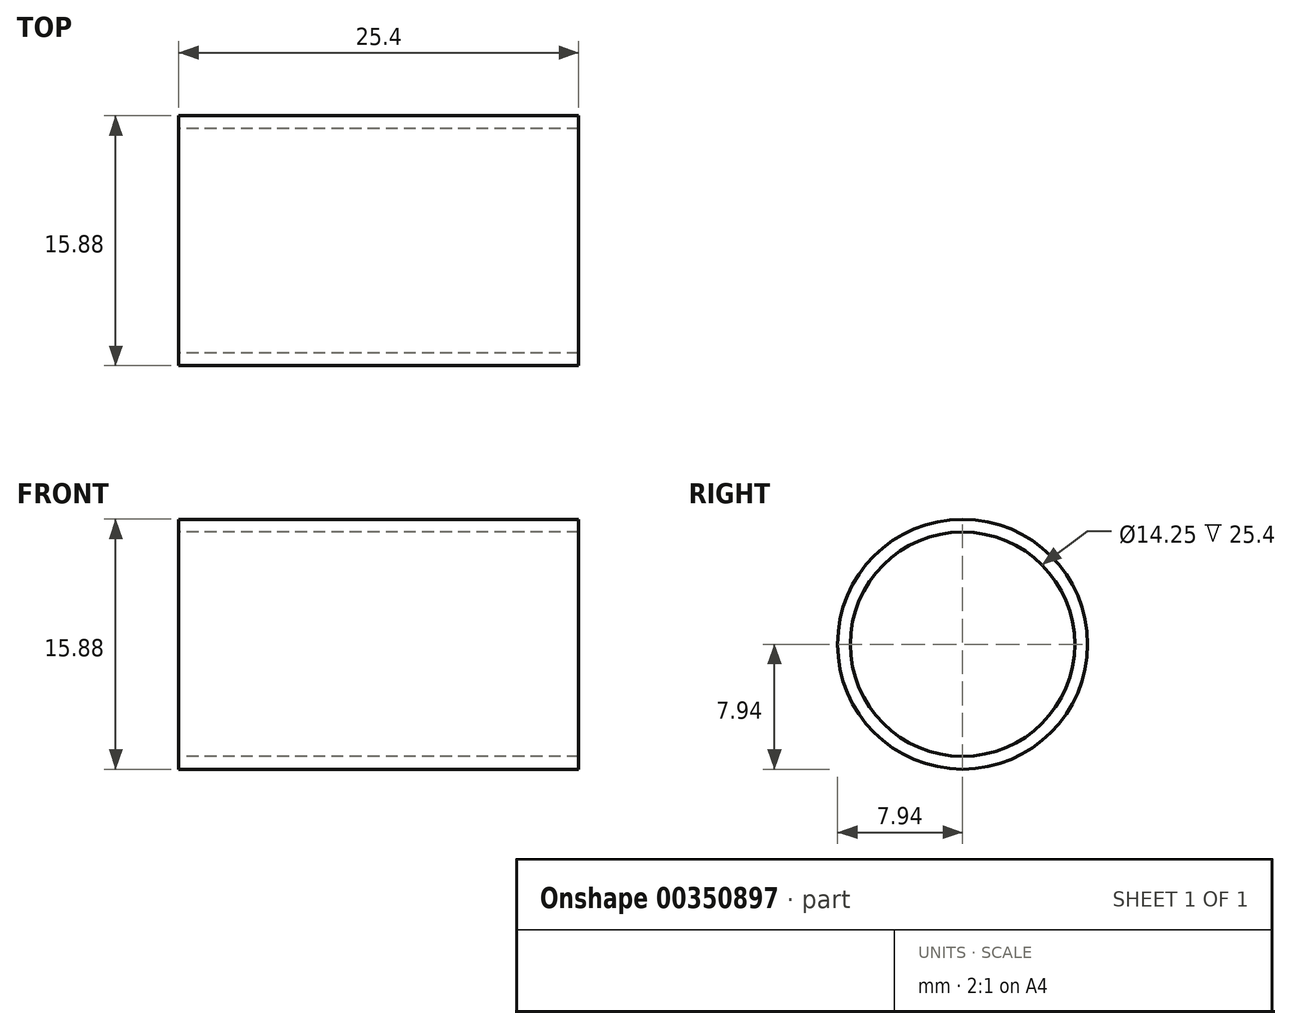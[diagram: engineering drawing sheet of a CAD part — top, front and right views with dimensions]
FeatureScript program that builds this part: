
annotation { "Feature Type Name" : "Feature", "Feature Type Description" : "" }
export const myFeature = defineFeature(function(context is Context, id is Id, definition is map)
    precondition{}
    {
        {
            var Q0;
            Q0=qCreatedBy(makeId("Right.planeOp"),FACE);
            var sketch = newSketch(context, id + "F0", { "sketchPlane" : qUnion([Q0])});
            skCircle(sketch, "E0", {"center": v(0, 0) * mm, "radius": 7.94 * mm});
            skCircle(sketch, "E1", {"center": v(0, 0) * mm, "radius": 7.12 * mm});
            skSolve(sketch);
        }
        {
            var Q0;
            Q0=qSketchRegion(id+"F0",true);
            extrude(context, id + "F1", {"entities" : qUnion([Q0]), "depth" : 25.4 * mm});
        }
    });
